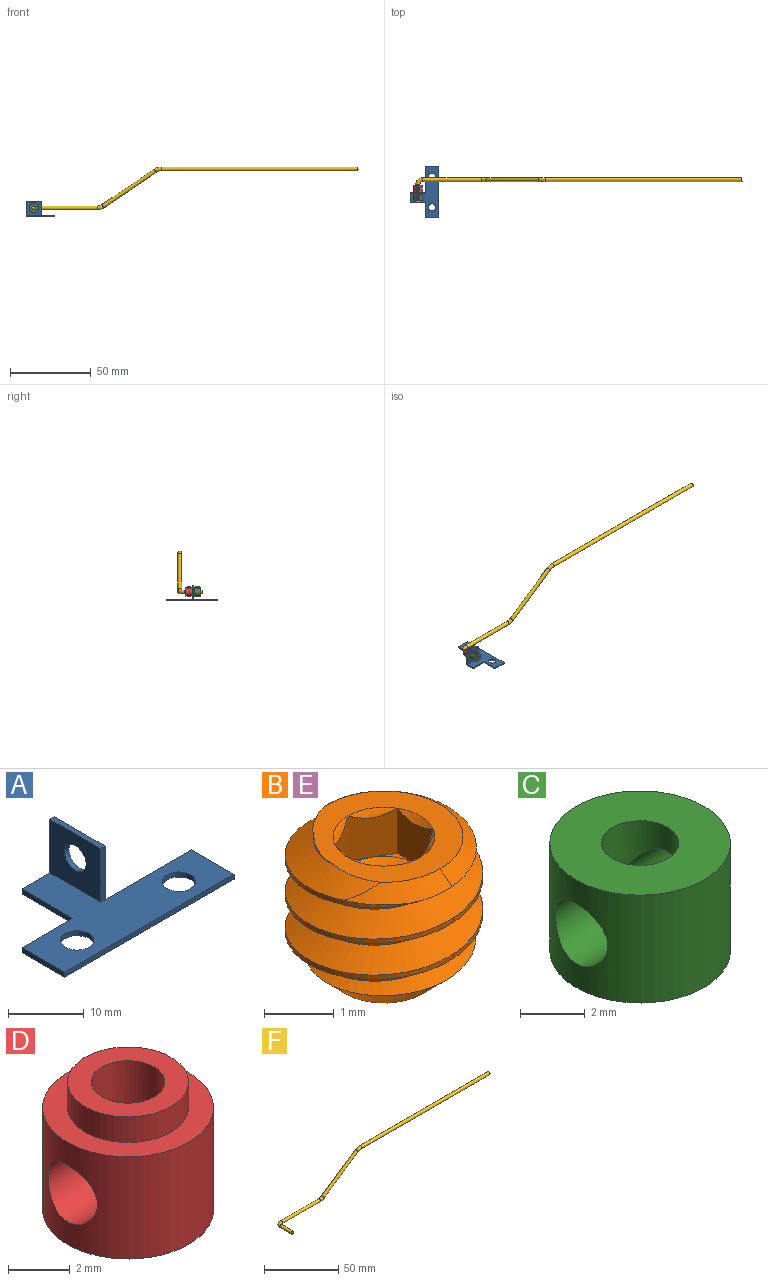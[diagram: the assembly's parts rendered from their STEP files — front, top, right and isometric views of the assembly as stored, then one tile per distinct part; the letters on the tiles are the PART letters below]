
ASSEMBLY  parts=6 mates=6
PART A: 16 faces, bbox 31.8x17.5x9.5 mm
  f0: plane 31.75x0.83mm, normal (0,-1,0), area 26.2mm2, adj f1,f7,f9,f10
  f1: plane 7.95x0.83mm, normal (1,0,0), area 6.6mm2, adj f0,f2,f9,f10
  f2: plane 16.18x0.83mm, normal (0,1,0), area 13.4mm2, adj f1,f9,f10,f12
  f3: plane 9.53x6.05mm, normal (0,1,0), area 12.2mm2, adj f4,f9,f10,f12,f13,f14
  f4: plane 9.53x0.83mm, normal (-1,0,0), area 7.9mm2, adj f3,f5,f9,f10
  f5: plane 9.53x0.83mm, normal (0,1,0), area 7.9mm2, adj f4,f7,f9,f10
  f6: cylinder r=2.22mm len=4.45mm, axis (0,0,-1), area 11.5mm2, adj f9,f10
  f7: plane 7.95x0.83mm, normal (-1,0,0), area 6.6mm2, adj f0,f5,f9,f10
  f8: cylinder r=2.22mm len=4.45mm, axis (0,0,-1), area 11.5mm2, adj f9,f10
  f9: plane 31.75x17.48mm, normal (0,0,1), area 271.1mm2, adj f0,f1,f2,f3,f4,f5,f6,f7
  f10: plane 31.75x17.48mm, normal (0,0,-1), area 279mm2, adj f0,f1,f2,f3,f4,f5,f6,f7
  f11: plane 8.7x0.83mm, normal (0,-1,0), area 7.2mm2, adj f9,f12,f13,f14
  f12: plane 9.53x9.53mm, normal (1,0,0), area 78.1mm2, adj f2,f3,f10,f11,f14,f15
  f13: plane 9.53x8.7mm, normal (-1,0,0), area 70.2mm2, adj f3,f9,f11,f14,f15
  f14: plane 9.53x0.83mm, normal (0,0,1), area 7.9mm2, adj f3,f11,f12,f13
  f15: cylinder r=2.01mm len=4.01mm, axis (1,0,0), area 10.4mm2, adj f12,f13
PART B: 36 faces, bbox 3.6x3.1x2.9 mm
  f0: cone r=0mm half-angle=59deg, axis (0,0,-1), area 2.2mm2, adj f1,f35
  f1: cone r=0mm half-angle=45deg, axis (0,0,1), area 2.3mm2, adj f0,f2,f31,f32,f33,f34,f35
  f2: cylinder r=1.42mm len=0.92mm, axis (0,0,1), area 0mm2, adj f1,f3,f34
  f3: cylinder r=1.42mm len=2.85mm, axis (0,0,1), area 0.4mm2, adj f2,f4,f31,f32,f34
  f4: cylinder r=1.42mm len=2.85mm, axis (0,0,1), area 0.4mm2, adj f3,f5,f32,f34
  f5: cylinder r=1.42mm len=2.85mm, axis (0,0,1), area 0.4mm2, adj f4,f6,f32,f34
  f6: cylinder r=1.42mm len=2.85mm, axis (0,0,1), area 0.4mm2, adj f5,f7,f32,f34
  f7: cylinder r=1.42mm len=2.73mm, axis (0,0,1), area 0.3mm2, adj f6,f8,f32,f34
  f8: cone r=0mm half-angle=55deg, axis (0,0,-1), area 0.4mm2, adj f7,f9,f11,f32,f34
  f9: cone r=0mm half-angle=55deg, axis (0,0,-1), area 0.6mm2, adj f8,f10,f11,f32
  f10: cone r=0mm half-angle=55deg, axis (0,0,-1), area 0mm2, adj f9,f11,f32
  f11: plane 2.29x2.19mm, normal (0,0,1), area 2.2mm2, adj f8,f9,f10,f12,f26,f27,f28,f29
  f12: cone r=0mm half-angle=45deg, axis (0,0,1), area 0mm2, adj f11,f13
  f13: plane 1.07x0.91mm, normal (0.5,-0.87,0), area 0.5mm2, adj f12,f14,f23,f24,f25
  f14: plane 1.07x0.91mm, normal (-0.5,-0.87,0), area 0.5mm2, adj f13,f15,f22,f23,f30
  f15: plane 0.87x0.8mm, normal (-1,0,0), area 0.5mm2, adj f14,f16,f21,f22,f29
  f16: plane 1.07x0.91mm, normal (-0.5,0.87,0), area 0.5mm2, adj f15,f17,f20,f21,f28
  f17: plane 1.07x0.91mm, normal (0.5,0.87,0), area 0.5mm2, adj f16,f18,f20,f25,f27
  f18: plane 0.55x0.32mm, normal (0,0,1), area 0mm2, adj f17,f19,f25
  f19: cone r=0mm half-angle=60deg, axis (0,0,1), area 1.5mm2, adj f18,f20,f21,f22,f23,f24
  f20: plane 0.64x0.18mm, normal (0,0,1), area 0mm2, adj f16,f17,f19
  f21: plane 0.55x0.32mm, normal (0,0,1), area 0mm2, adj f15,f16,f19
  f22: plane 0.55x0.32mm, normal (0,0,1), area 0mm2, adj f14,f15,f19
  f23: plane 0.64x0.18mm, normal (0,0,1), area 0mm2, adj f13,f14,f19
  f24: plane 0.55x0.32mm, normal (0,0,1), area 0mm2, adj f13,f19,f25
  f25: plane 1.07x1.01mm, normal (1,0,0), area 0.5mm2, adj f13,f17,f18,f24,f26
  f26: cone r=0mm half-angle=45deg, axis (0,0,1), area 0mm2, adj f11,f25
  f27: cone r=0mm half-angle=45deg, axis (0,0,1), area 0mm2, adj f11,f17
  f28: cone r=0mm half-angle=45deg, axis (0,0,1), area 0mm2, adj f11,f16
  f29: cone r=0mm half-angle=45deg, axis (0,0,1), area 0.1mm2, adj f11,f15
  f30: cone r=0mm half-angle=45deg, axis (0,0,1), area 0mm2, adj f11,f14
  f31: cone r=0mm half-angle=45deg, axis (0,0,1), area 0mm2, adj f1,f3,f32
  f32: bspline ~2.84x2.84mm, area 10.7mm2, adj f1,f3,f4,f5,f6,f7,f8,f9
  f33: cylinder r=1.01mm len=2.15mm, axis (0,0,-1), area 1.7mm2, adj f1,f11,f32,f34
  f34: bspline ~3.29x2.85mm, area 10.7mm2, adj f1,f2,f3,f4,f5,f6,f7,f8
  f35: cone r=0mm half-angle=45deg, axis (0,0,1), area 1.7mm2, adj f0,f1,f34
PART C: 6 faces, bbox 5.6x5.6x4.1 mm
  f0: cylinder r=1.19mm len=4.06mm, axis (0,0,1), area 20.9mm2, adj f2,f3,f4,f5
  f1: cylinder r=2.78mm len=5.56mm, axis (0,0,1), area 62.7mm2, adj f2,f3,f4,f5
  f2: plane 5.56x5.56mm, normal (0,0,-1), area 19.8mm2, adj f0,f1
  f3: plane 5.56x5.56mm, normal (0,0,1), area 19.8mm2, adj f0,f1
  f4: cylinder r=1.13mm len=2.39mm, axis (1,0,0), area 12.9mm2, adj f0,f1
  f5: cylinder r=1.13mm len=2.39mm, axis (-1,0,0), area 12.9mm2, adj f0,f1
PART D: 8 faces, bbox 5.6x5.6x5.1 mm
  f0: cylinder r=1.19mm len=5.08mm, axis (0,0,-1), area 28.5mm2, adj f3,f4,f6,f7
  f1: cylinder r=2.78mm len=5.56mm, axis (0,0,1), area 62.7mm2, adj f4,f5,f6,f7
  f2: cylinder r=1.97mm len=3.94mm, axis (0,0,-1), area 12.6mm2, adj f3,f5
  f3: plane 3.94x3.94mm, normal (0,0,1), area 7.7mm2, adj f0,f2
  f4: plane 5.56x5.56mm, normal (0,0,-1), area 19.8mm2, adj f0,f1
  f5: plane 5.56x5.56mm, normal (0,0,1), area 12.1mm2, adj f1,f2
  f6: cylinder r=1.13mm len=2.39mm, axis (1,0,0), area 12.9mm2, adj f0,f1
  f7: cylinder r=1.13mm len=2.39mm, axis (-1,0,0), area 12.9mm2, adj f0,f1
PART E: same geometry as B
PART F: 9 faces, bbox 202.2x15.5x27.7 mm
  f0: plane 2.36x2.36mm, normal (0,-1,0), area 4.4mm2, adj f2
  f1: plane 2.36x2.36mm, normal (1,0,0), area 4.4mm2, adj f8
  f2: cylinder r=1.18mm len=10.75mm, axis (0,1,0), area 79.8mm2, adj f0,f3
  f3: torus R=3.17mm, axis (0,0,-1), area 37mm2, adj f2,f4
  f4: cylinder r=1.18mm len=36.15mm, axis (1,0,0), area 268.3mm2, adj f3,f5
  f5: torus R=6.35mm, axis (0,-1,0), area 28.1mm2, adj f4,f6
  f6: cylinder r=1.18mm len=33.66mm, axis (0.83,0,0.56), area 290mm2, adj f5,f7
  f7: torus R=6.35mm, axis (0,1,0), area 28.1mm2, adj f6,f8
  f8: cylinder r=1.18mm len=121.87mm, axis (1,0,0), area 904.4mm2, adj f1,f7
PLACE A rot(axis=(0,0,1),90deg) t=(-21.81,-27.76,13.12)mm
PLACE B rot(axis=(0.02,-0.21,0.98),0deg) t=(-26.57,-31.15,20.95)mm
PLACE C rot(axis=(0.58,-0.58,0.58),120deg) t=(-26.57,-33.18,18.73)mm
PLACE D rot(axis=(0.58,0.58,-0.58),120deg) t=(-26.57,-27.97,18.73)mm
PLACE E t=(-26.57,-25.94,20.95)mm
PLACE F t=(-26.57,-27.81,18.73)mm
MATE slider A.f15 <-> F.f2  axis (0,-1,0) through (-26.57,-28.89,18.73)mm
MATE slider C.f4 <-> B.f0  axis (0,0,-1) through (-26.57,-31.15,20.31)mm
MATE slider D.f2 <-> F.f2  axis (0,-1,0) through (-26.57,-28.99,18.73)mm
MATE revolute C.f4 <-> B.f33  axis (0,0,-1) through (-26.57,-31.15,21.53)mm
MATE slider C.f1 <-> F.f2  axis (0,-1,0) through (-26.57,-33.18,18.73)mm
MATE revolute D.f6 <-> E.f0  axis (0,0,-1) through (-26.57,-25.94,21.53)mm
